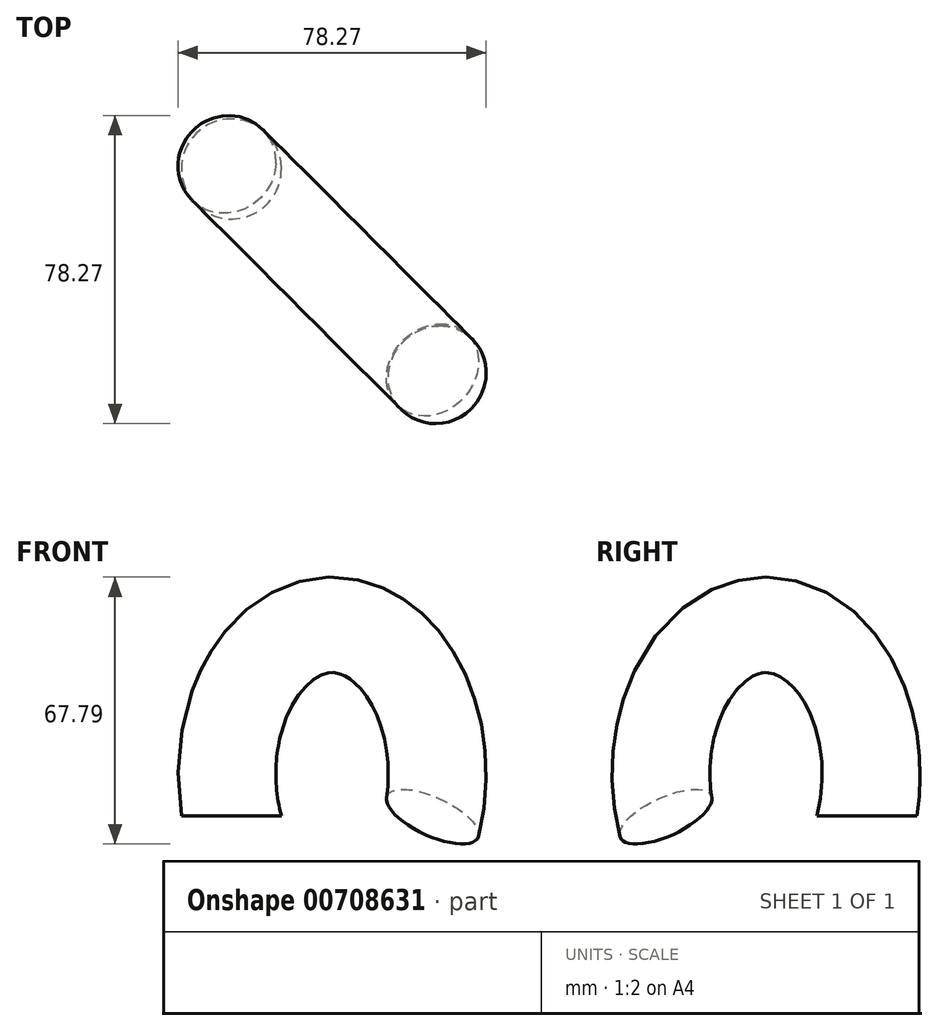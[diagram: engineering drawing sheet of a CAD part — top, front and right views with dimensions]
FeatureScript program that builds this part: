
annotation { "Feature Type Name" : "Feature", "Feature Type Description" : "" }
export const myFeature = defineFeature(function(context is Context, id is Id, definition is map)
    precondition{}
    {
        {
            var Q0;
            Q0=qCreatedBy(makeId("Top.planeOp"),FACE);
            var sketch = newSketch(context, id + "F0", { "sketchPlane" : qUnion([Q0])});
            skCircle(sketch, "E0", {"center": v(0, 0) * mm, "radius": 22.44 * mm});
            skSolve(sketch);
        }
        {
            var Q0;
            Q0=qCreatedBy(makeId("Top.planeOp"),FACE);
            var sketch = newSketch(context, id + "F1", { "sketchPlane" : qUnion([Q0])});
            skCircle(sketch, "E1", {"center": v(-50.8, 50.8) * mm, "radius": 12.7 * mm});
            skSolve(sketch);
        }
        {
            var Q0;
            Q0=qCreatedBy(makeId("Front.planeOp"),FACE);
            var sketch = newSketch(context, id + "F2", { "sketchPlane" : qUnion([Q0])});
            skLineSegment(sketch, "E2", {"start": v(0, 0) * mm, "end": v(0, 72.64) * mm});
            skSolve(sketch);
        }
        {
            var Q0;
            Q0=qCreatedBy(makeId("Right.planeOp"),FACE);
            var Q1;
            Q1=sQuery(id+"F2.wireOp",EDGE,"E2");
            cPlane(context, id + "F3", {"entities" : qUnion([Q0, Q1]), "cplaneType" : CPlaneType.LINE_ANGLE, "offset" : 25.4 * mm, "angle" : 45 * degree, "width" : 152.4 * mm, "height" : 152.4 * mm});
        }
        {
            var Q0;
            Q0=qCreatedBy(id+"F3.planeOp",FACE);
            var sketch = newSketch(context, id + "F4", { "sketchPlane" : qUnion([Q0])});
            skArc(sketch, "E3", {"start": v(0, 0) * mm, "mid": v(-35.69, 47.84) * mm, "end": v(-71.38, 0) * mm});
            skSolve(sketch);
        }
        {
            var Q0;
            Q0=makeQuery(id+"F1.imprint","IMPRINT",FACE,{"disambiguationData":[TD([[makeQuery(id+"F1.imprint","IMPRINT",EDGE,{"derivedFrom":sQuery(id+"F1.wireOp",EDGE,"E1")}),1.0]])]});
            var Q1;
            Q1=sQuery(id+"F4.wireOp",EDGE,"E3");
            sweep(context, id + "F5", {"profiles" : qUnion([Q0]), "path" : qUnion([Q1])});
        }
    });
